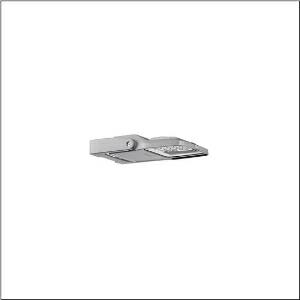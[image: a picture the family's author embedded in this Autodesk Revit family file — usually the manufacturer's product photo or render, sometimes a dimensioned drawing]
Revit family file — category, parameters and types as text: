
# Revit family: floodlight_fl_21_iq_micro___pl52_5xa7762a4d2a_e4f8
name_source: partatom
category: Lighting Fixtures
units: mm (PartAtom-declared; Revit-internal decimal feet)

## family parameters
Cut with Voids When Loaded = No
Host = Face
Light Source = No
Part Type = Normal
Room Calculation Point = No
Round Connector Dimension = Use Diameter
Shared = No

## types (1)
- --- (1 x LED, 3010 lm, 23.1 W, 4000K)
    Apparent Load = 23 VA
    CIE Flux Codes = 26 60 98 100 100
    Color Rendering = 70
    Color Temperature = 4000K
    Default Elevation = 1800 mm
    Description = Floodlight FL 21 iQ micro, floodlight, primary light control with lens, of PMMA, primary optical cover: protective disc, of toughened safety glass, transparent, light distribution: PL52, light emission: direct distribution, installation type: surface-mounted, LED, High Power LED, rated luminous flux: 3.010lm, luminous efficacy: 130lm/W, light colour: 740, colour temperature: 4000K, control gear: iQ Street-Remote/DALI, control: Auto-Match, Temp-Guard, Night-Set, Smart-Wire, Desk-Remote (wireless, voltage-free reading and setting of iQ features in the workshop via application-optimized NFC function/RFID function), optimised constant luminous flux control (CLO 2.0), Street-Remote, with terminal, 6-pole, mains connection: 220..240V, AC, 50/60Hz, start of lifetime: 23W, end of service life: 24W, reduction: 11W, luminaire housing, of diecast aluminium, powder-coated, Siteco® metallic grey (DB 702S), corrosivity category C5 mid according to DIN EN ISO 12944, suitable for swimming pools, chlorine-resistant, sealing non-destructively replaceable, design bracket, of diecast aluminium, powder-coated, Siteco® metallic grey (DB 702S), protection rating (complete): IP66, insulation class (complete): insulation class II (safety insulation), certification: CE, ENEC, VDE, protection symbol: D, impact resistance: IK07, permissible operating ambient temperature: -40..+40°C, permissible operating ambient temperature for outdoor applications: -40..+50°C, standard: DIN EN 12944, LABS conformity tested according to VDMA 24364:2018-05, packaging unit: 1 piece

Light Distribution: PL52
    Height = 65 mm
    Lamp = 1 x LED
    Lamp Light Flux = 3010 lm
    Lamp Power = 23.1 W
    Lamp count = 1
    Length = 312 mm
    Luminous efficacy = 130 lm/W
    Manufacturer = Siteco
    ModVariant = No
    Model = 5XA7762A4D2A
    Mounting Place = Wall
    Mounting Type = Surface mounted
    Number of Poles = 1
    OnlyDefault = Yes
    Power Factor = 1
    Product Name = Floodlight FL 21 iQ micro | PL52
    Product group = floodlight | wall mounted
    ProductGroupID = 2001
    Protection Class = Protection class II
    Protection Degree = IP 66
    RLX_Detail_Level = 1
    RLX_Emergency_Light_Flux = 0 lm
    RLX_Emergency_Type = 0
    RLX_Emergency_Type_DB = No
    RlxData = <blob elided: 97681 chars, md5=ef55018c>
    Socket = socket
    Standby Power = 0 W
    System Light Flux = 3010 lm
    System Power = 23 W
    Type Comments = factory setting: luminous flux: 100 % | dim-lin: 254 | 455 mA
    Type Image = l_1006878.jpg
    URL = http://relux.com
    VarID = @adj_177774
    Voltage = 0 V
    Weight = 0.00 kg
    Width = 230 mm

## geometry (parser evidence)
native form markers: Blend x4, Sweep x12
no freeform markers — native parametric forms only
